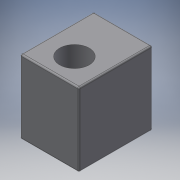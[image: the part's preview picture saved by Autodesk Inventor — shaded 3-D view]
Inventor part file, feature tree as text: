
AUTODESK INVENTOR PART (.ipt)
format: ipt  version: 2018 (Build 220112000, 112)  size: 139,776 bytes
history: native  units: in
note: dims shown in document units (in); Inventor stores cm internally (conversion verified against a paired STEP export)
features: extrude x4, sketch x4, other x2, fillet x1, reference x1
ambient origin geometry x8: Origin, YZ Plane, XZ Plane, XY Plane, X Axis, Y Axis, Z Axis, Center Point
bodies: Solid1 (feature_tree)
feature tree (12):
  extrude  "Extrusion1"  Depth=314.9606in
  fillet  "Fillet1"  Radius=393.7008in
  extrude  "Extrusion2"  Depth=7.874in
  extrude  "Extrusion3"  Depth=157.4803in
  extrude  "Extrusion4"  Depth=157.4803in
  sketch  "Sketch1"  dims[d0=393.7008in d1=314.9606in d2=393.7008in d3=0.0in]
  sketch  "Sketch2"  dims[d4=7.874in d5=177.1654in]
  reference  "Reference1"
  sketch  "Sketch3"  dims[d6=39.3701in d7=0.0in d8=157.4803in]
  sketch  "Sketch4"  dims[d9=157.4803in d10=0.0in d12=19.685in d13=157.4803in d14=0.0in]
  other  "Assembly1"
  other  "base rotor:1"
